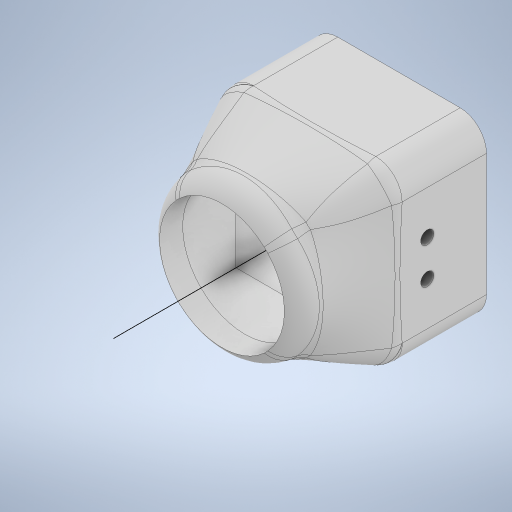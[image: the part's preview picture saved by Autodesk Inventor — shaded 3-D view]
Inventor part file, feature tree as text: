
AUTODESK INVENTOR PART (.ipt)
format: ipt  version: 2023 (Build 270158000, 158)  size: 823,808 bytes
history: native  units: in
note: dims shown in document units (in); Inventor stores cm internally (conversion verified against a paired STEP export)
features: sketch x17, extrude x12, projected_geometry x10, plane x2, loft x2, fillet x2
ambient origin geometry x8: Origin, YZ Plane, XZ Plane, XY Plane, X Axis, Y Axis, Z Axis, Center Point
bodies: Solid1 (feature_tree), Solid3 (feature_tree)
feature tree (45):
  extrude  "Extrusion1"  Depth=0.874in
  extrude  "Extrusion2"  Depth=0.6299in
  sketch  "Sketch3"  dims[d5=0.2854in d6=0.0in d9=0.2165in]
  extrude  "Extrusion4"  Depth=0.2165in
  extrude  "Extrusion5"  Depth=0.2165in
  extrude  "Extrusion6"  Depth=0.374in
  extrude  "Extrusion8"  Depth=0.0886in TaperAngle=0.0deg
  extrude  "Extrusion9"  Depth=0.2362in TaperAngle=0.0deg
  extrude  "Extrusion10"  Depth=0.1378in TaperAngle=0.0deg
  sketch  "Sketch12"  dims[d41=0.4409in d48=0.3543in]
  plane  "Work Plane2"
  extrude  "Extrusion12"  Depth=0.0394in
  plane  "Work Plane4"
  sketch  "Sketch18"  dims[d52=0.1083in d53=0.0787in]
  extrude  "Extrusion14"  Depth=0.3543in
  extrude  "Extrusion15"  Depth=0.0787in
  sketch  "Sketch22"  dims[d65=0.3937in d66=0.0in]
  sketch  "Sketch23"  dims[d67=0.0787in]
  loft  "Loft2"
  loft  "Loft3"
  fillet  "Fillet3"  Radius=0.0079in
  fillet  "Fillet4"  Radius=0.3937in
  extrude  "Extrusion16"  Depth=0.0787in
  sketch  "Sketch1"  dims[d0=0.874in d1=0.874in]
  sketch  "Sketch2"  dims[d2=0.315in d3=0.0in d4=0.6299in]
  projected_geometry  "Projected Loop1"
  sketch  "Sketch5"  dims[d10=0.0886in d11=0.0in d12=0.2165in]
  projected_geometry  "Projected Loop3"
  sketch  "Sketch6"  dims[d13=0.0886in d14=0.0in d15=0.374in]
  projected_geometry  "Projected Loop4"
  sketch  "Sketch7"  dims[d16=0.0886in d17=0.0in d23=0.0886in d24=0.0in]
  projected_geometry  "Projected Loop5"
  sketch  "Sketch9"  dims[d25=0.0787in d26=0.2362in d27=0.0in]
  projected_geometry  "Projected Loop8"
  sketch  "Sketch10"  dims[d28=0.7307in d29=0.1378in d30=0.0in]
  projected_geometry  "Projected Loop9"
  sketch  "Sketch11"  dims[d31=1.063in d36=0.0394in]
  sketch  "Sketch17"  dims[d49=0.1083in d50=0.0787in]
  projected_geometry  "Projected Loop11"
  sketch  "Sketch20"  dims[d54=0.0in d55=0.0in d56=-0.437in d60=0.0079in d61=0.3937in d62=0.0in]
  projected_geometry  "Projected Loop13"
  sketch  "Sketch21"  dims[d63=0.0079in d64=0.0787in]
  projected_geometry  "Projected Loop14"
  projected_geometry  "Projected Loop15"
  sketch  "Sketch24"  dims[d68=0.0in d69=90.0deg d70=0.0in d71=90.0deg d72=0.0in d73=90.0deg d74=0.0in d75=90.0deg d76=0.1575in d77=0.1575in d78=0.0in d79=0.0in]
